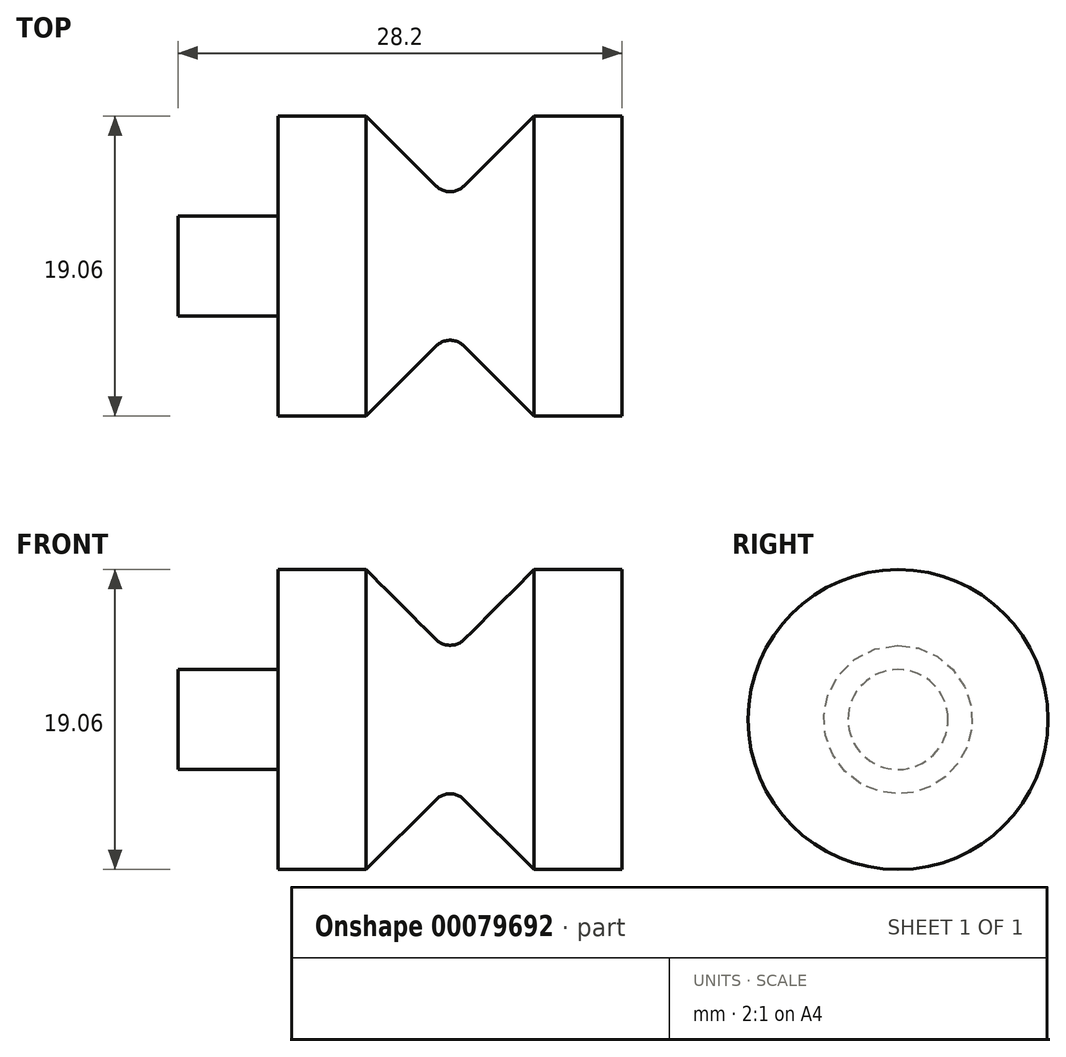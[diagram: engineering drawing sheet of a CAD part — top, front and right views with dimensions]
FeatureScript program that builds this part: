
annotation { "Feature Type Name" : "Feature", "Feature Type Description" : "" }
export const myFeature = defineFeature(function(context is Context, id is Id, definition is map)
    precondition{}
    {
        {
            var Q0;
            Q0=qCreatedBy(makeId("Front.planeOp"),FACE);
            var sketch = newSketch(context, id + "F0", { "sketchPlane" : qUnion([Q0])});
            skLineSegment(sketch, "E0", {"start": v(-3.21, 0) * mm, "end": v(-3.21, 9.52) * mm});
            skLineSegment(sketch, "E1", {"start": v(-3.21, 9.53) * mm, "end": v(-8.8, 9.53) * mm});
            skLineSegment(sketch, "E2", {"start": v(-8.8, 9.52) * mm, "end": v(-13.24, 5.09) * mm});
            skLineSegment(sketch, "E3", {"start": v(-15.03, 5.09) * mm, "end": v(-19.47, 9.53) * mm});
            skLineSegment(sketch, "E4", {"start": v(-19.47, 9.53) * mm, "end": v(-25.06, 9.53) * mm});
            skLineSegment(sketch, "E5", {"start": v(-25.06, 9.53) * mm, "end": v(-25.06, 3.18) * mm});
            skLineSegment(sketch, "E6", {"start": v(-25.06, 3.18) * mm, "end": v(-31.4, 3.18) * mm});
            skLineSegment(sketch, "E7", {"start": v(-31.4, 3.18) * mm, "end": v(-31.4, 0) * mm});
            skLineSegment(sketch, "E8.MirrorCS", {"start": v(-8.8, -9.52) * mm, "end": v(-13.24, -5.09) * mm, "construction": true});
            skLineSegment(sketch, "E9.MirrorCS", {"start": v(-15.03, -5.09) * mm, "end": v(-19.47, -9.53) * mm, "construction": true});
            skLineSegment(sketch, "E10.MirrorCS", {"start": v(-19.47, -9.53) * mm, "end": v(-25.06, -9.53) * mm, "construction": true});
            skLineSegment(sketch, "E11.MirrorCS", {"start": v(-25.06, -9.53) * mm, "end": v(-25.06, -3.18) * mm, "construction": true});
            skLineSegment(sketch, "E12.MirrorCS", {"start": v(-3.21, 0) * mm, "end": v(-3.21, -9.52) * mm, "construction": true});
            skLineSegment(sketch, "E13.MirrorCS", {"start": v(-25.06, -3.18) * mm, "end": v(-31.4, -3.18) * mm, "construction": true});
            skLineSegment(sketch, "E14.MirrorCS", {"start": v(-3.21, -9.52) * mm, "end": v(-8.8, -9.52) * mm, "construction": true});
            skLineSegment(sketch, "E15.MirrorCS", {"start": v(-31.4, -3.18) * mm, "end": v(-31.4, 0) * mm, "construction": true});
            skLineSegment(sketch, "E16", {"start": v(-48.5, 0) * mm, "end": v(-39.8, 0) * mm, "construction": true});
            skLineSegment(sketch, "E17", {"start": v(-31.4, 0) * mm, "end": v(-3.21, 0) * mm});
            skLineSegment(sketch, "E18", {"start": v(-27.4, 24.23) * mm, "end": v(-27.4, -24.3) * mm, "construction": true});
            skLineSegment(sketch, "E19", {"start": v(-19.47, -9.53) * mm, "end": v(-8.8, -9.52) * mm, "construction": true});
            skPoint(sketch, "E20", {"position": v(-14.13, -9.53) * mm});
            skLineSegment(sketch, "E21", {"start": v(-14.13, -4.2) * mm, "end": v(-14.13, -9.53) * mm, "construction": true});
            skPoint(sketch, "E22.visualSharp", {"position": v(-14.13, 4.2) * mm});
            skArc(sketch, "E22.filletArc", {"start": v(-15.03, 5.09) * mm, "mid": v(-14.13, 4.72) * mm, "end": v(-13.24, 5.09) * mm});
            skPoint(sketch, "E23.visualSharp", {"position": v(-14.13, -4.2) * mm});
            skArc(sketch, "E23.filletArc", {"start": v(-13.24, -5.09) * mm, "mid": v(-14.13, -4.72) * mm, "end": v(-15.03, -5.09) * mm, "construction": true});
            skSolve(sketch);
        }
        {
            var Q0;
            Q0=makeQuery(id+"F0.imprint","IMPRINT",FACE,{"disambiguationData":[TD([[makeQuery(id+"F0.imprint","IMPRINT",EDGE,{"derivedFrom":sQuery(id+"F0.wireOp",EDGE,"E0")}),1.0]])]});
            var Q1;
            Q1=sQuery(id+"F0.wireOp",EDGE,"E16");
            revolve(context, id + "F1", {"entities" : qUnion([Q0]), "axis" : qUnion([Q1]), "revolveType" : RevolveType.FULL});
        }
    });
